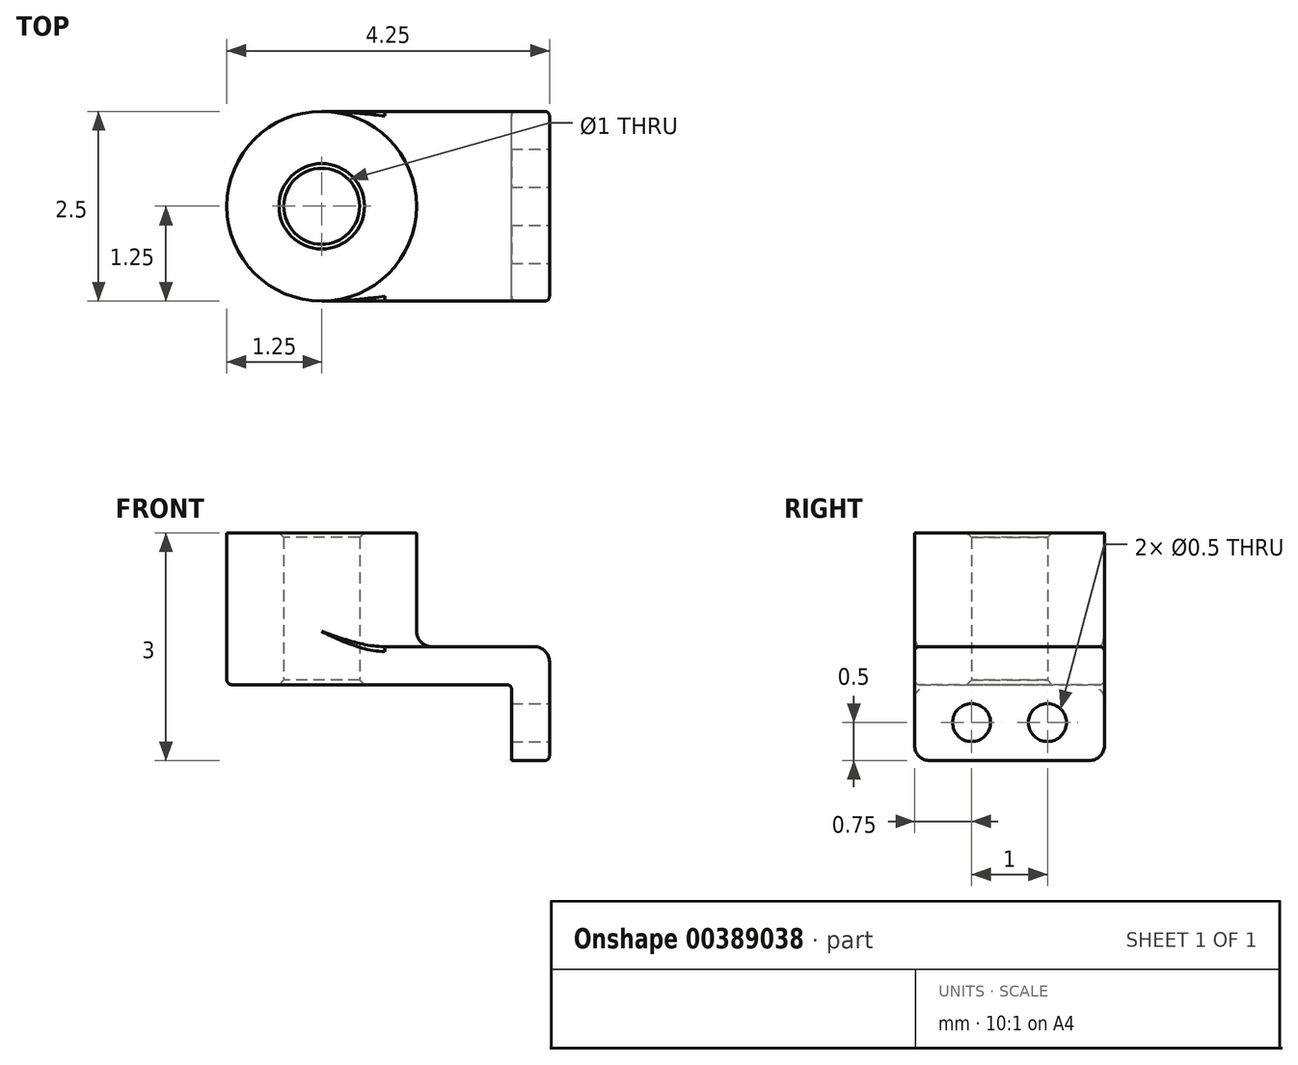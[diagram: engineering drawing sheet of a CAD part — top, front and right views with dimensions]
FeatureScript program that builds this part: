
annotation { "Feature Type Name" : "Feature", "Feature Type Description" : "" }
export const myFeature = defineFeature(function(context is Context, id is Id, definition is map)
    precondition{}
    {
        {
            var Q0;
            Q0=qCreatedBy(makeId("Top.planeOp"),FACE);
            var sketch = newSketch(context, id + "F0", { "sketchPlane" : qUnion([Q0])});
            skLineSegment(sketch, "E0.bottom", {"start": v(1.5, 1.25) * mm, "end": v(-1.5, 1.25) * mm});
            skLineSegment(sketch, "E0.top", {"start": v(1.5, -1.25) * mm, "end": v(-1.5, -1.25) * mm});
            skLineSegment(sketch, "E0.left", {"start": v(1.5, 1.25) * mm, "end": v(1.5, -1.25) * mm});
            skLineSegment(sketch, "E0.right", {"start": v(-1.5, 1.25) * mm, "end": v(-1.5, -1.25) * mm});
            skPoint(sketch, "E0.middle", {"position": v(0, 0) * mm});
            skCircle(sketch, "E1", {"center": v(-1.5, 0) * mm, "radius": 1.25 * mm});
            skCircle(sketch, "E2", {"center": v(-1.5, 0) * mm, "radius": 0.5 * mm});
            skSolve(sketch);
        }
        {
            var Q0;
            Q0 = qSketchRegion(id + "F0", true);
            extrude(context, id + "F1", {"entities" : qUnion([Q0]), "depth" : 0.5 * mm});
        }
        {
            var Q0;
            {var subQ1=sQuery(id+"F0.wireOp",EDGE,"E0.right");var subQ3=sQuery(id+"F0.wireOp",EDGE,"E2");var subQ4=makeQuery(id+"F0.imprint","INTERSECT",VERTEX,{"disambiguationData":[OD(0.0)],"derivedFrom":[subQ1,subQ3]});Q0=makeQuery(id+"F0.imprint","IMPRINT",FACE,{"disambiguationData":[TD([[makeQuery(id+"F0.imprint","IMPRINT",EDGE,{"disambiguationData":[TD([[subQ4,-1.0]])],"derivedFrom":subQ3}),-1.0]])]});}
            var Q1;
            {var subQ1=sQuery(id+"F0.wireOp",EDGE,"E0.right");var subQ3=sQuery(id+"F0.wireOp",EDGE,"E2");var subQ4=makeQuery(id+"F0.imprint","INTERSECT",VERTEX,{"disambiguationData":[OD(0.0)],"derivedFrom":[subQ1,subQ3]});Q1=makeQuery(id+"F0.imprint","IMPRINT",FACE,{"disambiguationData":[TD([[makeQuery(id+"F0.imprint","IMPRINT",EDGE,{"disambiguationData":[TD([[subQ4,1.0]])],"derivedFrom":subQ3}),-1.0]])]});}
            extrude(context, id + "F2", {"entities" : qUnion([Q0, Q1]), "operationType" : NewBodyOperationType.ADD, "depth" : 2 * mm});
        }
        {
            var Q0;
            Q0=makeQuery(id+"F1.opExtrude","SWEPT_FACE",FACE,{"disambiguationData":[OSD([sQuery(id+"F0.wireOp",EDGE,"E0.left")])]});
            var sketch = newSketch(context, id + "F3", { "sketchPlane" : qUnion([Q0])});
            skCircle(sketch, "E3", {"center": v(-0.5, -0.5) * mm, "radius": 0.25 * mm});
            skLineSegment(sketch, "E4.bottom", {"start": v(-1.25, 0.5) * mm, "end": v(1.25, 0.5) * mm});
            skLineSegment(sketch, "E4.top", {"start": v(-1.25, -1) * mm, "end": v(1.25, -1) * mm});
            skLineSegment(sketch, "E4.left", {"start": v(-1.25, 0.5) * mm, "end": v(-1.25, -1) * mm});
            skLineSegment(sketch, "E4.right", {"start": v(1.25, 0.5) * mm, "end": v(1.25, -1) * mm});
            skLineSegment(sketch, "E5", {"start": v(0, 0) * mm, "end": v(0, -1) * mm, "construction": true});
            skCircle(sketch, "E6.MirrorC", {"center": v(0.5, -0.5) * mm, "radius": 0.25 * mm});
            skSolve(sketch);
        }
        {
            var Q0;
            Q0 = qSketchRegion(id + "F3", true);
            extrude(context, id + "F4", {"entities" : qUnion([Q0]), "operationType" : NewBodyOperationType.ADD, "oppositeDirection" : true, "depth" : .5 * mm});
        }
        {
            var Q0;
            {var subQ0=sQuery(id+"F0.wireOp",EDGE,"E1");Q0=makeQuery(id+"F2.boolean.opBoolean","INTERSECT",EDGE,{"derivedFrom":[makeQuery(id+"F1.opExtrude","CAP_FACE",FACE,{"disambiguationData":[OSD([sQuery(id+"F0.wireOp",EDGE,"E0.bottom"),sQuery(id+"F0.wireOp",EDGE,"E0.top"),sQuery(id+"F0.wireOp",EDGE,"E0.left"),subQ0,sQuery(id+"F0.wireOp",EDGE,"E2")])],"isStart":false}),makeQuery(id+"F2.opExtrude","SWEPT_FACE",FACE,{"disambiguationData":[OSD([subQ0])]})]});}
            var Q1;
            Q1=makeQuery(id+"F1.opExtrude","CAP_EDGE",EDGE,{"disambiguationData":[OSD([sQuery(id+"F0.wireOp",EDGE,"E0.left")])],"isStart":false});
            var Q2;
            Q2=makeQuery(id+"F4.opExtrude","SWEPT_EDGE",EDGE,{"disambiguationData":[OSD([sQuery(id+"F3.wireOp",EDGE,"E4.top"),sQuery(id+"F3.wireOp",EDGE,"E4.left")])]});
            var Q3;
            Q3=makeQuery(id+"F4.opExtrude","SWEPT_EDGE",EDGE,{"disambiguationData":[OSD([sQuery(id+"F3.wireOp",EDGE,"E4.top"),sQuery(id+"F3.wireOp",EDGE,"E4.right")])]});
            fillet(context, id + "F5", {"entities" : qUnion([Q0, Q1, Q2, Q3]), "radius" : .2 * mm, "tangentPropagation" : true, "allowEdgeOverflow" : false});
        }
        {
            var Q0;
            Q0=makeQuery(id+"F1.opExtrude","CAP_EDGE",EDGE,{"disambiguationData":[OSD([sQuery(id+"F0.wireOp",EDGE,"E0.top")])],"isStart":true});
            var Q1;
            Q1=makeQuery(id+"F4.boolean.opBoolean","INTERSECT",EDGE,{"derivedFrom":[makeQuery(id+"F1.opExtrude","CAP_FACE",FACE,{"disambiguationData":[OSD([sQuery(id+"F0.wireOp",EDGE,"E0.bottom"),sQuery(id+"F0.wireOp",EDGE,"E0.top"),sQuery(id+"F0.wireOp",EDGE,"E0.left"),sQuery(id+"F0.wireOp",EDGE,"E1"),sQuery(id+"F0.wireOp",EDGE,"E2")])],"isStart":true}),makeQuery(id+"F4.opExtrude","CAP_FACE",FACE,{"disambiguationData":[OSD([sQuery(id+"F3.wireOp",EDGE,"E3"),sQuery(id+"F3.wireOp",EDGE,"E4.bottom"),sQuery(id+"F3.wireOp",EDGE,"E4.top"),sQuery(id+"F3.wireOp",EDGE,"E4.left"),sQuery(id+"F3.wireOp",EDGE,"E4.right"),sQuery(id+"F3.wireOp",EDGE,"E6.MirrorC")])],"isStart":false})]});
            var Q2;
            Q2=makeQuery(id+"F1.opExtrude","CAP_EDGE",EDGE,{"disambiguationData":[OSD([sQuery(id+"F0.wireOp",EDGE,"E0.top")])],"isStart":false});
            fillet(context, id + "F6", {"entities" : qUnion([Q0, Q1, Q2]), "radius" : (1 / 16) * mm, "tangentPropagation" : true, "allowEdgeOverflow" : false});
        }
        {
            var Q0;
            {var subQ0=sQuery(id+"F0.wireOp",EDGE,"E2");Q0=makeQuery(id+"F2.boolean.opBoolean","MERGE",FACE,{"derivedFrom":[makeQuery(id+"F1.opExtrude","SWEPT_FACE",FACE,{"disambiguationData":[OSD([subQ0])]}),makeQuery(id+"F2.opExtrude","SWEPT_FACE",FACE,{"disambiguationData":[OSD([subQ0])]})]});}
            chamfer(context, id + "F7", {"entities" : qUnion([Q0]), "width" : (1 / 16) * mm, "tangentPropagation" : true});
        }
    });
